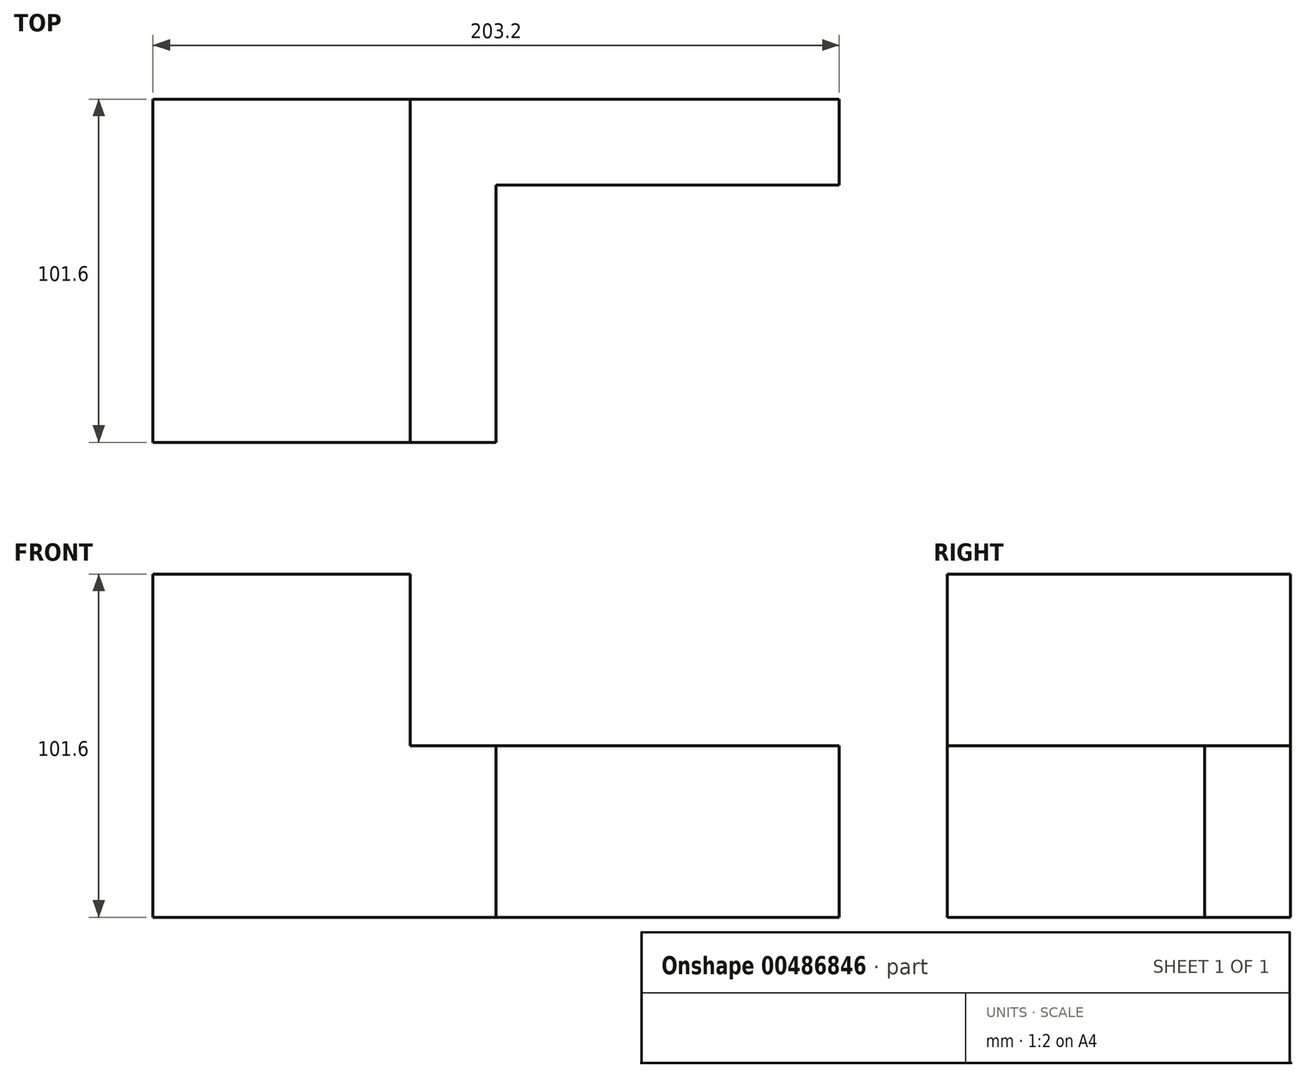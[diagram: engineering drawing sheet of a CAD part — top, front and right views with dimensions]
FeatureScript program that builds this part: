
annotation { "Feature Type Name" : "Feature", "Feature Type Description" : "" }
export const myFeature = defineFeature(function(context is Context, id is Id, definition is map)
    precondition{}
    {
        {
            var Q0;
            Q0=qCreatedBy(makeId("Front.planeOp"),FACE);
            var sketch = newSketch(context, id + "F0", { "sketchPlane" : qUnion([Q0])});
            skLineSegment(sketch, "E0.bottom", {"start": v(0, 0) * mm, "end": v(-203.2, 0) * mm});
            skLineSegment(sketch, "E0.top", {"start": v(-127, 101.6) * mm, "end": v(-203.2, 101.6) * mm});
            skLineSegment(sketch, "E0.left", {"start": v(0, 0) * mm, "end": v(0, 50.8) * mm});
            skLineSegment(sketch, "E0.right", {"start": v(-203.2, 0) * mm, "end": v(-203.2, 101.6) * mm});
            skLineSegment(sketch, "E1.top", {"start": v(0, 50.8) * mm, "end": v(-127, 50.8) * mm});
            skLineSegment(sketch, "E1.right", {"start": v(-127, 101.6) * mm, "end": v(-127, 50.8) * mm});
            skSolve(sketch);
        }
        {
            var Q0;
            Q0 = qSketchRegion(id + "F0", true);
            extrude(context, id + "F1", {"entities" : qUnion([Q0]), "depth" : 101.6 * mm});
        }
        {
            var Q0;
            Q0=makeQuery(id+"F1.opExtrude","SWEPT_FACE",FACE,{"disambiguationData":[OSD([sQuery(id+"F0.wireOp",EDGE,"E1.top")])]});
            var sketch = newSketch(context, id + "F2", { "sketchPlane" : qUnion([Q0])});
            skLineSegment(sketch, "E2.bottom", {"start": v(0, -101.6) * mm, "end": v(-101.6, -101.6) * mm});
            skLineSegment(sketch, "E2.top", {"start": v(0, -25.4) * mm, "end": v(-101.6, -25.4) * mm});
            skLineSegment(sketch, "E2.left", {"start": v(0, -101.6) * mm, "end": v(0, -25.4) * mm});
            skLineSegment(sketch, "E2.right", {"start": v(-101.6, -101.6) * mm, "end": v(-101.6, -25.4) * mm});
            skSolve(sketch);
        }
        {
            var Q0;
            Q0 = qSketchRegion(id + "F2", true);
            extrude(context, id + "F3", {"entities" : qUnion([Q0]), "operationType" : NewBodyOperationType.REMOVE, "oppositeDirection" : true, "depth" : 101.6 * mm});
        }
    });
